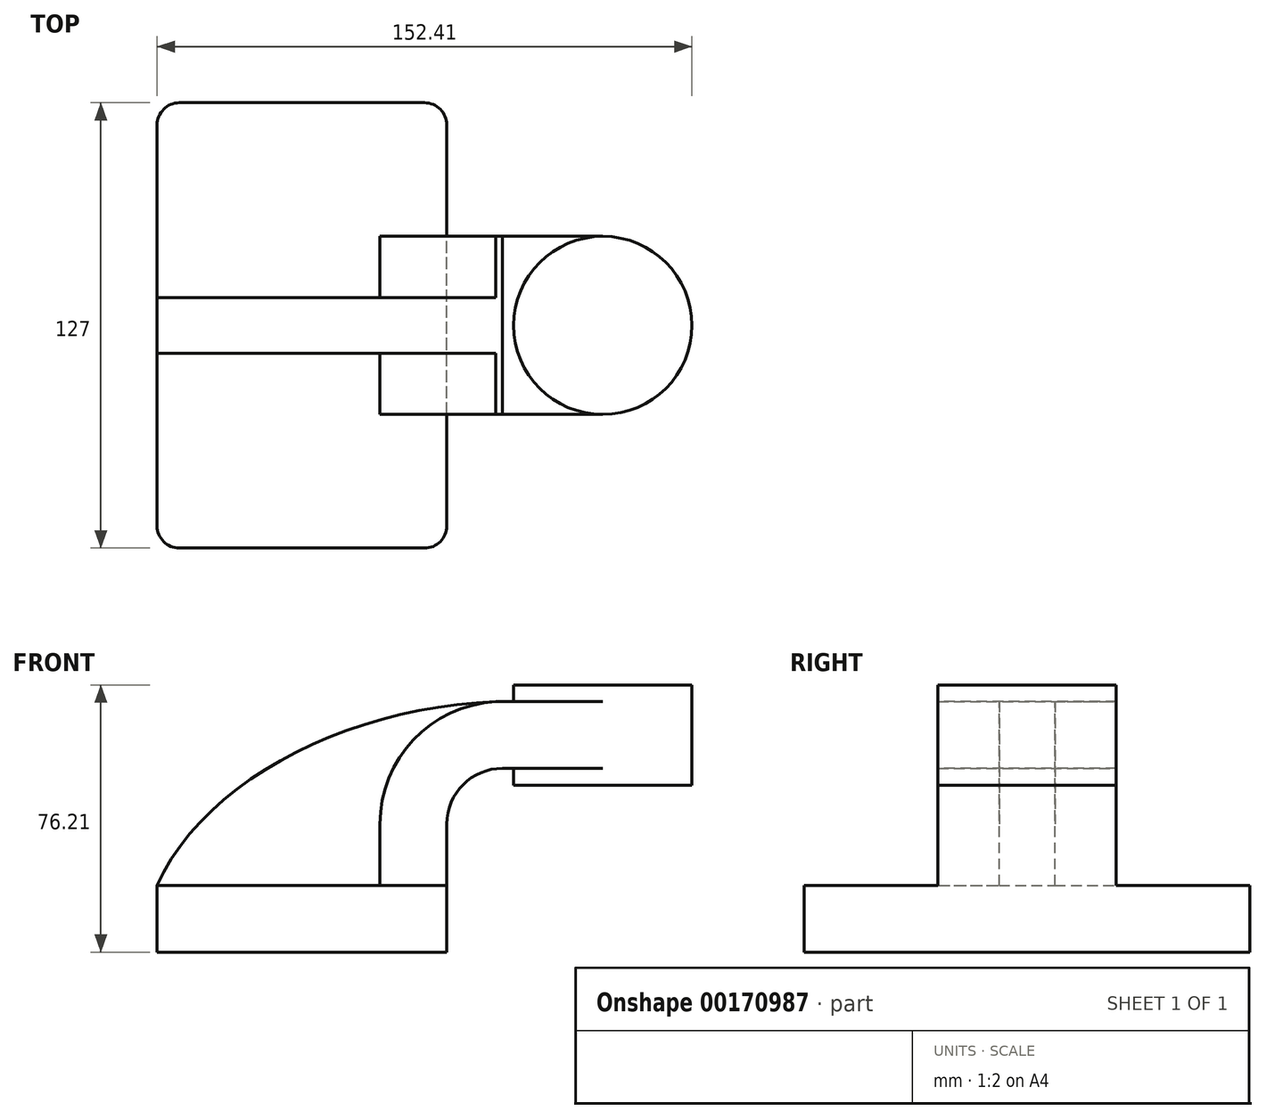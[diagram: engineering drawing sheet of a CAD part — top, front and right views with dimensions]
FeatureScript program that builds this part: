
annotation { "Feature Type Name" : "Feature", "Feature Type Description" : "" }
export const myFeature = defineFeature(function(context is Context, id is Id, definition is map)
    precondition{}
    {
        {
            var Q0;
            Q0=qCreatedBy(makeId("Front.planeOp"),FACE);
            var sketch = newSketch(context, id + "F0", { "sketchPlane" : qUnion([Q0])});
            skLineSegment(sketch, "E0.bottom", {"start": v(41.27, 9.53) * mm, "end": v(-41.28, 9.53) * mm});
            skLineSegment(sketch, "E0.top", {"start": v(41.28, -9.52) * mm, "end": v(-41.27, -9.52) * mm});
            skLineSegment(sketch, "E0.left", {"start": v(41.28, 9.53) * mm, "end": v(41.28, -9.52) * mm});
            skLineSegment(sketch, "E0.right", {"start": v(-41.28, 9.53) * mm, "end": v(-41.27, -9.52) * mm});
            skPoint(sketch, "E0.middle", {"position": v(0, 0) * mm});
            skLineSegment(sketch, "E1.bottom", {"start": v(111.13, 38.1) * mm, "end": v(60.33, 38.1) * mm});
            skLineSegment(sketch, "E1.top", {"start": v(111.13, 66.68) * mm, "end": v(60.32, 66.68) * mm});
            skLineSegment(sketch, "E1.left", {"start": v(111.12, 38.1) * mm, "end": v(111.12, 66.68) * mm});
            skLineSegment(sketch, "E1.right", {"start": v(60.32, 38.1) * mm, "end": v(60.32, 66.68) * mm});
            skPoint(sketch, "E1.middle", {"position": v(85.73, 52.39) * mm});
            skLineSegment(sketch, "E2", {"start": v(41.27, 9.53) * mm, "end": v(41.27, 27) * mm});
            skArc(sketch, "E3", {"start": v(41.28, 27) * mm, "mid": v(45.92, 38.23) * mm, "end": v(57.15, 42.88) * mm});
            skArc(sketch, "E4.1", {"start": v(22.23, 27) * mm, "mid": v(32.45, 51.7) * mm, "end": v(57.15, 61.93) * mm});
            skLineSegment(sketch, "E4.2", {"start": v(22.22, 9.53) * mm, "end": v(22.22, 27) * mm});
            skLineSegment(sketch, "E5", {"start": v(57.15, 42.88) * mm, "end": v(85.72, 42.88) * mm});
            skPoint(sketch, "E5.endSnap0", {"position": v(85.73, 38.1) * mm});
            skLineSegment(sketch, "E6", {"start": v(57.15, 61.93) * mm, "end": v(85.72, 61.93) * mm});
            skLineSegment(sketch, "E7", {"start": v(85.72, 66.68) * mm, "end": v(85.72, 38.1) * mm});
            skFitSpline(sketch, "E8", {"points": [v(-41.28, 9.53) * mm, v(57.15, 61.93) * mm], "startDerivative": vector(40.2, 90.22) * mm, "endDerivative": vector(129, 2.66) * mm});
            skSolve(sketch);
        }
        {
            var Q0;
            Q0=makeQuery(id+"F0.imprint","IMPRINT",FACE,{"disambiguationData":[TD([[makeQuery(id+"F0.imprint","IMPRINT",EDGE,{"derivedFrom":sQuery(id+"F0.wireOp",EDGE,"E0.top")}),-1.0]])]});
            extrude(context, id + "F1", {"entities" : qUnion([Q0]), "endBound" : BoundingType.SYMMETRIC, "depth" : 127 * mm});
        }
        {
            var Q0;
            {var subQ4=sQuery(id+"F0.wireOp",EDGE,"E2");Q0=makeQuery(id+"F0.imprint","IMPRINT",FACE,{"disambiguationData":[TD([[makeQuery(id+"F0.imprint","IMPRINT",EDGE,{"derivedFrom":subQ4}),1.0]])]});}
            var Q1;
            {var subQ0=sQuery(id+"F0.wireOp",EDGE,"E5");var subQ1=sQuery(id+"F0.wireOp",EDGE,"E1.right");var subQ2=makeQuery(id+"F0.imprint","INTERSECT",VERTEX,{"derivedFrom":[subQ1,subQ0]});Q1=makeQuery(id+"F0.imprint","IMPRINT",FACE,{"disambiguationData":[TD([[makeQuery(id+"F0.imprint","IMPRINT",EDGE,{"disambiguationData":[TD([[subQ2,-1.0]])],"derivedFrom":subQ1}),-1.0]])]});}
            extrude(context, id + "F2", {"entities" : qUnion([Q0, Q1]), "operationType" : NewBodyOperationType.ADD, "endBound" : BoundingType.SYMMETRIC, "depth" : 50.8 * mm});
        }
        {
            var Q0;
            {var subQ3=sQuery(id+"F0.wireOp",EDGE,"E4.2");Q0=makeQuery(id+"F0.imprint","IMPRINT",FACE,{"disambiguationData":[TD([[makeQuery(id+"F0.imprint","IMPRINT",EDGE,{"derivedFrom":subQ3}),1.0]])]});}
            extrude(context, id + "F3", {"entities" : qUnion([Q0]), "operationType" : NewBodyOperationType.ADD, "endBound" : BoundingType.SYMMETRIC, "depth" : 15.88 * mm});
        }
        {
            var Q0;
            {var subQ0=sQuery(id+"F0.wireOp",EDGE,"E1.left");Q0=makeQuery(id+"F0.imprint","IMPRINT",FACE,{"disambiguationData":[TD([[makeQuery(id+"F0.imprint","IMPRINT",EDGE,{"derivedFrom":subQ0}),1.0]])]});}
            var Q1;
            Q1=sQuery(id+"F0.wireOp",EDGE,"E7");
            revolve(context, id + "F4", {"operationType" : NewBodyOperationType.ADD, "entities" : qUnion([Q0]), "axis" : qUnion([Q1]), "revolveType" : RevolveType.FULL});
        }
        {
            var Q0;
            Q0=makeQuery(id+"F1.opExtrude","CAP_EDGE",EDGE,{"disambiguationData":[OSD([sQuery(id+"F0.wireOp",EDGE,"E0.left")])],"isStart":false});
            var Q1;
            Q1=makeQuery(id+"F1.opExtrude","CAP_EDGE",EDGE,{"disambiguationData":[OSD([sQuery(id+"F0.wireOp",EDGE,"E0.right")])],"isStart":false});
            var Q2;
            Q2=makeQuery(id+"F1.opExtrude","CAP_EDGE",EDGE,{"disambiguationData":[OSD([sQuery(id+"F0.wireOp",EDGE,"E0.right")])],"isStart":true});
            var Q3;
            Q3=makeQuery(id+"F1.opExtrude","CAP_EDGE",EDGE,{"disambiguationData":[OSD([sQuery(id+"F0.wireOp",EDGE,"E0.left")])],"isStart":true});
            fillet(context, id + "F5", {"entities" : qUnion([Q0, Q1, Q2, Q3]), "radius" : 6.35 * mm, "tangentPropagation" : true, "allowEdgeOverflow" : false});
        }
    });
